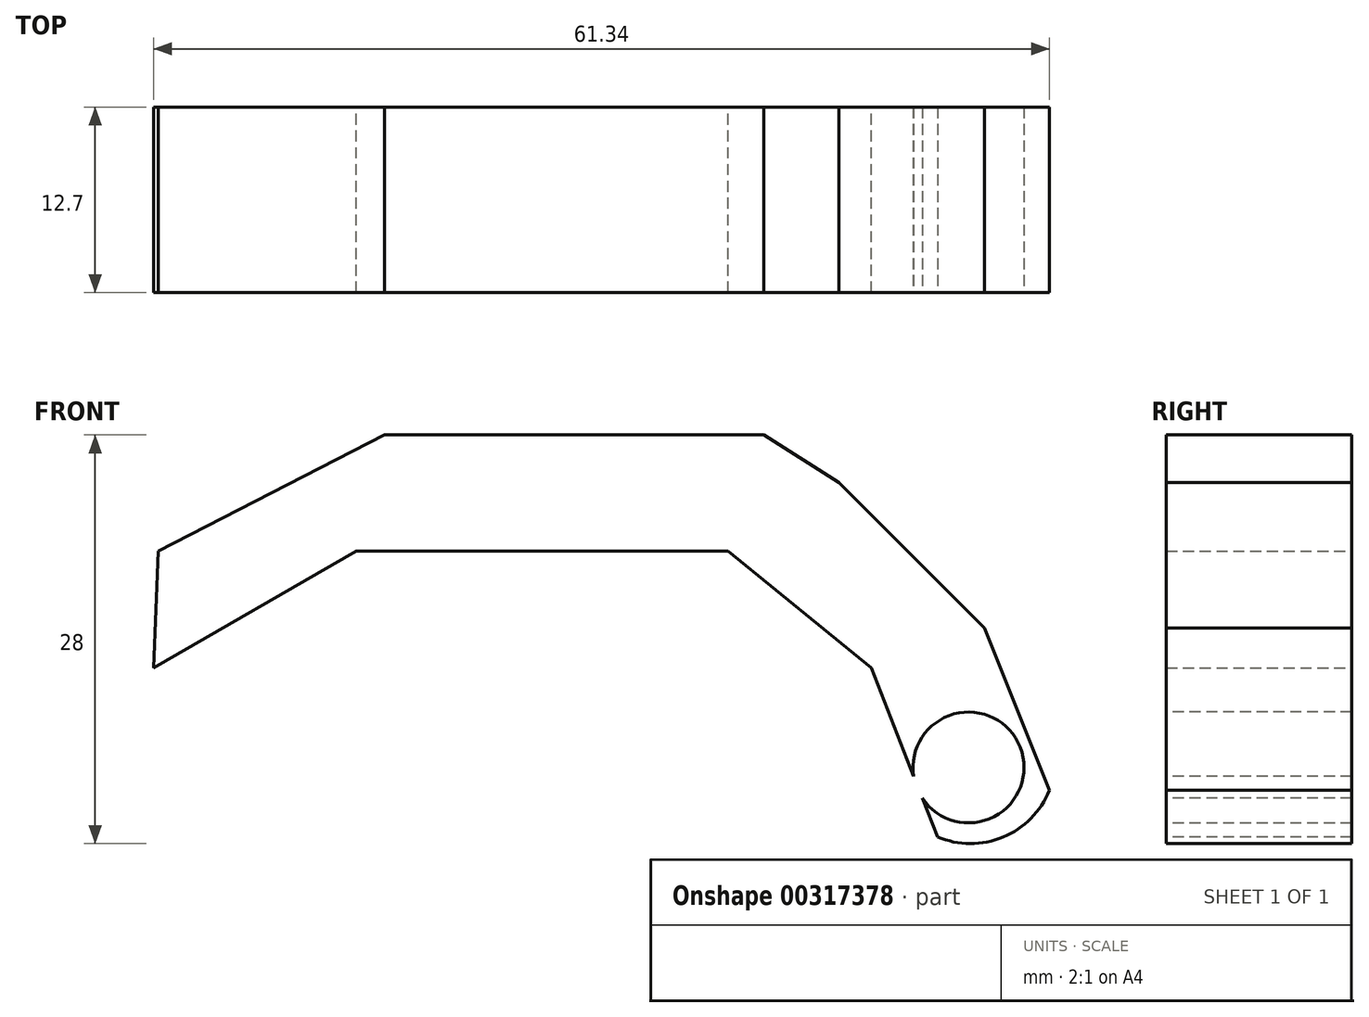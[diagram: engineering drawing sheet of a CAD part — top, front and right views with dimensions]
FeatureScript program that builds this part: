
annotation { "Feature Type Name" : "Feature", "Feature Type Description" : "" }
export const myFeature = defineFeature(function(context is Context, id is Id, definition is map)
    precondition{}
    {
        {
            var Q0;
            Q0=qCreatedBy(makeId("Front.planeOp"),FACE);
            var sketch = newSketch(context, id + "F0", { "sketchPlane" : qUnion([Q0])});
            skLineSegment(sketch, "E0", {"start": v(-1.93, 0) * mm, "end": v(-23.69, 0) * mm});
            skLineSegment(sketch, "E1", {"start": v(-23.69, 0) * mm, "end": v(-37.55, -7.98) * mm});
            skLineSegment(sketch, "E2", {"start": v(-1.93, 0) * mm, "end": v(1.77, 0) * mm});
            skLineSegment(sketch, "E3", {"start": v(1.77, 0) * mm, "end": v(11.6, -7.98) * mm});
            skLineSegment(sketch, "E4", {"start": v(11.6, -7.98) * mm, "end": v(19.34, -27.8) * mm});
            skLineSegment(sketch, "E5", {"start": v(19.34, -27.8) * mm, "end": v(23.6, -21.09) * mm});
            skLineSegment(sketch, "E6", {"start": v(-37.55, -7.98) * mm, "end": v(-37.24, 0) * mm});
            skLineSegment(sketch, "E7", {"start": v(-37.24, 0) * mm, "end": v(-21.75, 7.98) * mm});
            skLineSegment(sketch, "E8", {"start": v(-21.75, 7.98) * mm, "end": v(4.23, 7.98) * mm});
            skLineSegment(sketch, "E9", {"start": v(4.23, 7.98) * mm, "end": v(9.39, 4.7) * mm});
            skLineSegment(sketch, "E10", {"start": v(9.39, 4.7) * mm, "end": v(19.34, -5.25) * mm});
            skPoint(sketch, "E11.start.orphan", {"position": v(-21.75, 6.04) * mm});
            skPoint(sketch, "E12.end.orphan", {"position": v(4.23, 6.04) * mm});
            skPoint(sketch, "E13.end.orphan", {"position": v(19.34, -7.5) * mm});
            skLineSegment(sketch, "E14", {"start": v(19.34, -5.25) * mm, "end": v(24.06, -17.07) * mm});
            skLineSegment(sketch, "E15", {"start": v(24.06, -17.07) * mm, "end": v(23.6, -21.09) * mm});
            skSolve(sketch);
        }
        {
            var Q0;
            Q0=makeQuery(id+"F0.imprint","IMPRINT",FACE,{"disambiguationData":[TD([[makeQuery(id+"F0.imprint","IMPRINT",EDGE,{"derivedFrom":sQuery(id+"F0.wireOp",EDGE,"E0")}),-1.0]])]});
            extrude(context, id + "F1", {"entities" : qUnion([Q0]), "depth" : 12.7 * mm});
        }
        {
            var Q0;
            Q0=makeQuery(id+"F1.opExtrude","CAP_FACE",FACE,{"disambiguationData":[OSD([sQuery(id+"F0.wireOp",EDGE,"E0"),sQuery(id+"F0.wireOp",EDGE,"E1"),sQuery(id+"F0.wireOp",EDGE,"E2"),sQuery(id+"F0.wireOp",EDGE,"E3"),sQuery(id+"F0.wireOp",EDGE,"E4"),sQuery(id+"F0.wireOp",EDGE,"E5"),sQuery(id+"F0.wireOp",EDGE,"GwV2uBuL-wj1r-OLJ7-1em4-mu4Xt5tnTymT"),sQuery(id+"F0.wireOp",EDGE,"E6"),sQuery(id+"F0.wireOp",EDGE,"E7"),sQuery(id+"F0.wireOp",EDGE,"E8"),sQuery(id+"F0.wireOp",EDGE,"E9"),sQuery(id+"F0.wireOp",EDGE,"E10"),sQuery(id+"F0.wireOp",EDGE,"E13")])],"isStart":false});
            var sketch = newSketch(context, id + "F2", { "sketchPlane" : qUnion([Q0])});
            skLineSegment(sketch, "E16", {"start": v(0, 0) * mm, "end": v(18.25, -14.8) * mm});
            skSolve(sketch);
        }
        {
            var Q0;
            Q0=sQuery(id+"F2.wireOp",VERTEX,"E16.end");
            var Q1;
            Q1=makeQuery(id+"F1.opExtrude","SWEPT_BODY",BODY,{"disambiguationData":[OSD([sQuery(id+"F0.wireOp",EDGE,"E0"),sQuery(id+"F0.wireOp",EDGE,"E1"),sQuery(id+"F0.wireOp",EDGE,"E2"),sQuery(id+"F0.wireOp",EDGE,"E3"),sQuery(id+"F0.wireOp",EDGE,"E4"),sQuery(id+"F0.wireOp",EDGE,"E5"),sQuery(id+"F0.wireOp",EDGE,"GwV2uBuL-wj1r-OLJ7-1em4-mu4Xt5tnTymT"),sQuery(id+"F0.wireOp",EDGE,"E6"),sQuery(id+"F0.wireOp",EDGE,"E7"),sQuery(id+"F0.wireOp",EDGE,"E8"),sQuery(id+"F0.wireOp",EDGE,"E9"),sQuery(id+"F0.wireOp",EDGE,"E10"),sQuery(id+"F0.wireOp",EDGE,"E13")])]});
            hole(context, id + "F3", {"style" : HoleStyle.SIMPLE, "endStyle" : HoleEndStyle.THROUGH, "holeDiameter" : 7.6 * mm, "tappedDepth" : 12.7 * mm, "tapClearance" : 3, "locations" : qUnion([Q0]), "scope" : qUnion([Q1])});
        }
        {
            var Q0;
            Q0=makeQuery(id+"F1.opExtrude","CAP_FACE",FACE,{"disambiguationData":[OSD([sQuery(id+"F0.wireOp",EDGE,"E0"),sQuery(id+"F0.wireOp",EDGE,"E1"),sQuery(id+"F0.wireOp",EDGE,"E2"),sQuery(id+"F0.wireOp",EDGE,"E3"),sQuery(id+"F0.wireOp",EDGE,"E4"),sQuery(id+"F0.wireOp",EDGE,"E5"),sQuery(id+"F0.wireOp",EDGE,"E6"),sQuery(id+"F0.wireOp",EDGE,"E7"),sQuery(id+"F0.wireOp",EDGE,"E8"),sQuery(id+"F0.wireOp",EDGE,"E9"),sQuery(id+"F0.wireOp",EDGE,"E10"),sQuery(id+"F0.wireOp",EDGE,"E14"),sQuery(id+"F0.wireOp",EDGE,"E15")])],"isStart":false});
            var sketch = newSketch(context, id + "F4", { "sketchPlane" : qUnion([Q0])});
            skArc(sketch, "E17", {"start": v(16.13, -19.57) * mm, "mid": v(20.62, -19.58) * mm, "end": v(23.79, -16.38) * mm});
            skSolve(sketch);
        }
        {
            var Q0;
            {var subQ4=sQuery(id+"F4.wireOp",EDGE,"E17");Q0=makeQuery(id+"F4.imprint","IMPRINT",FACE,{"disambiguationData":[TD([[makeQuery(id+"F4.imprint","IMPRINT",EDGE,{"derivedFrom":subQ4}),-1.0]])]});}
            extrude(context, id + "F5", {"entities" : qUnion([Q0]), "operationType" : NewBodyOperationType.REMOVE, "oppositeDirection" : true, "depth" : 25.4 * mm});
        }
    });
